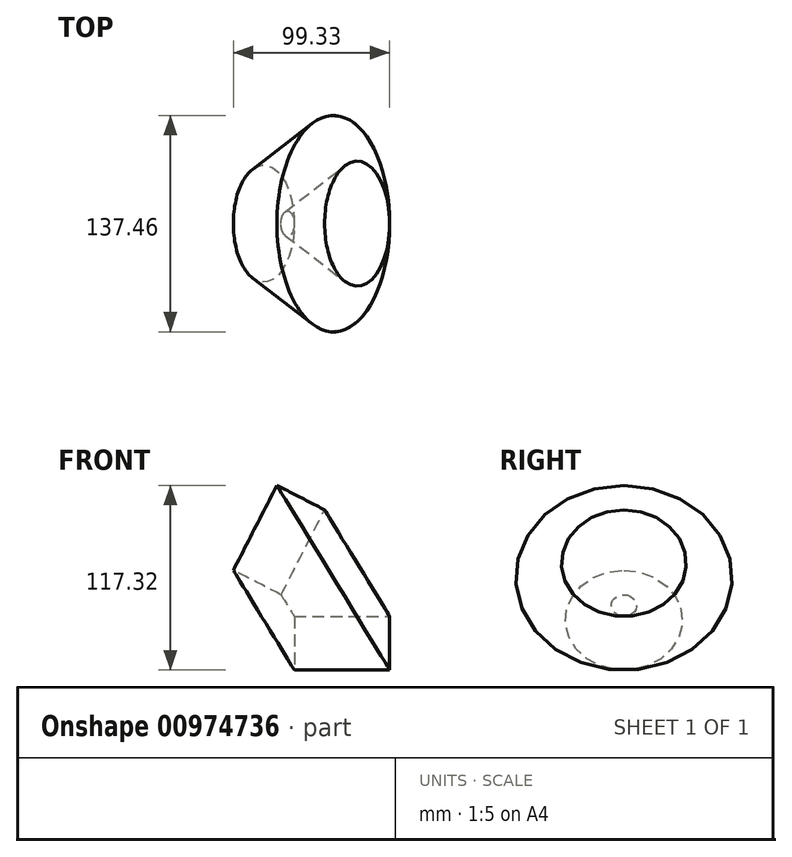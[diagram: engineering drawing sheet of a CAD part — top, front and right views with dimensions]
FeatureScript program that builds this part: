
annotation { "Feature Type Name" : "Feature", "Feature Type Description" : "" }
export const myFeature = defineFeature(function(context is Context, id is Id, definition is map)
    precondition{}
    {
        {
            var Q0;
            Q0=qCreatedBy(makeId("Front.planeOp"),FACE);
            var sketch = newSketch(context, id + "F0", { "sketchPlane" : qUnion([Q0])});
            skLineSegment(sketch, "E0.bottom", {"start": v(0, 0) * mm, "end": v(60.62, 0) * mm});
            skLineSegment(sketch, "E0.top", {"start": v(0, -34.06) * mm, "end": v(60.62, -34.06) * mm});
            skLineSegment(sketch, "E0.left", {"start": v(0, 0) * mm, "end": v(0, -34.06) * mm});
            skLineSegment(sketch, "E0.right", {"start": v(60.62, 0) * mm, "end": v(60.62, -34.06) * mm});
            skLineSegment(sketch, "E1", {"start": v(35.01, 30.84) * mm, "end": v(87.64, 63) * mm, "construction": true});
            skSolve(sketch);
        }
        {
            var Q0;
            Q0 = qSketchRegion(id + "F0", true);
            var Q1;
            Q1=sQuery(id+"F0.wireOp",EDGE,"E1");
            revolve(context, id + "F1", {"surfaceOperationType" : NewSurfaceOperationType.NEW, "entities" : qUnion([Q0]), "axis" : qUnion([Q1]), "revolveType" : RevolveType.FULL});
        }
    });
